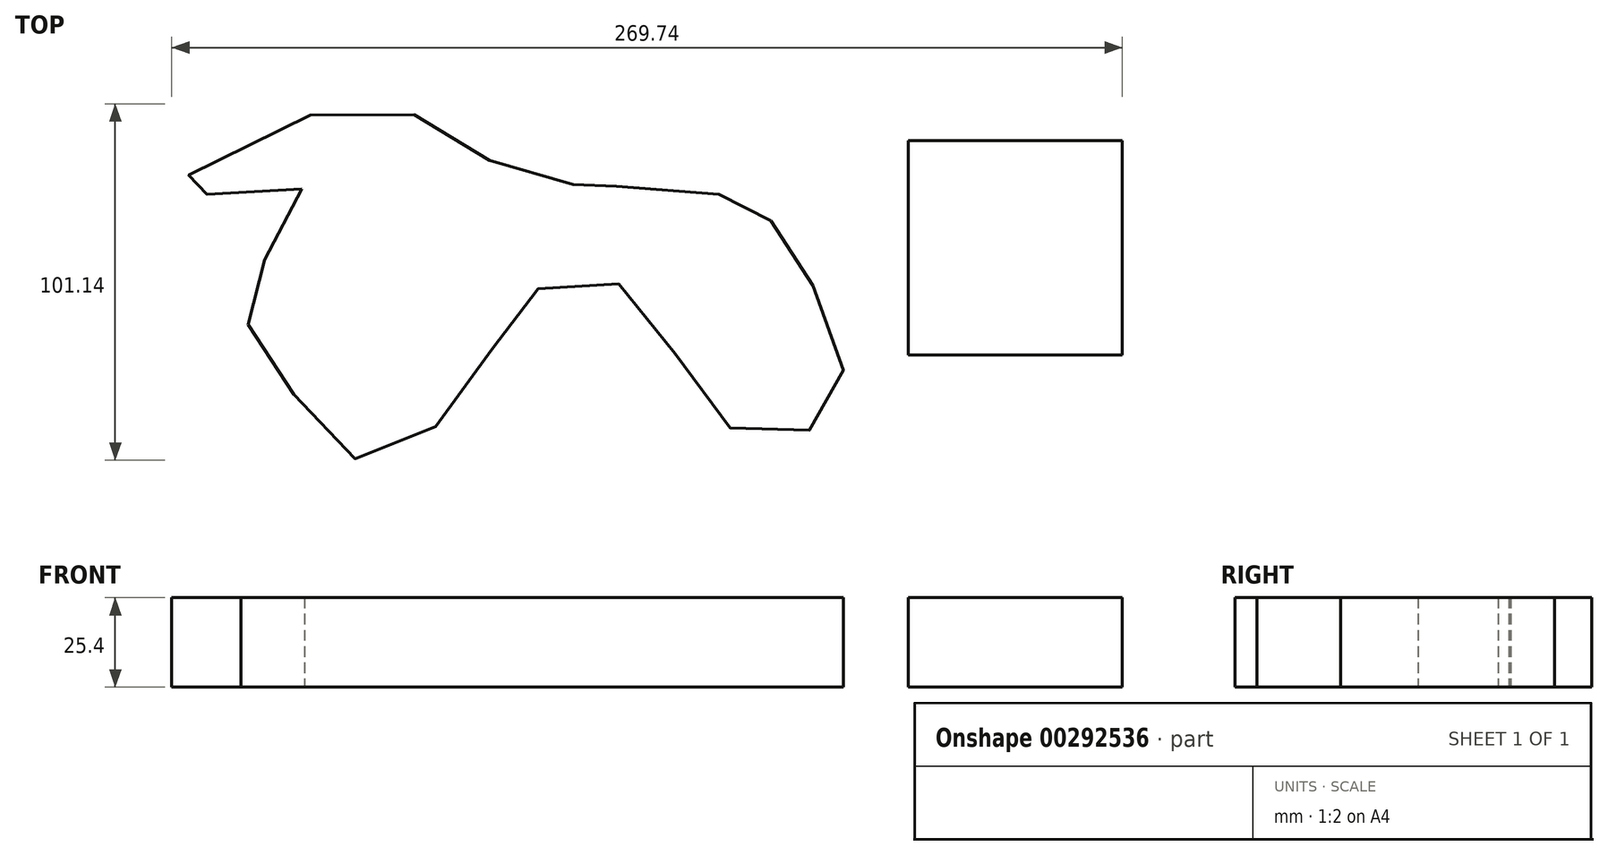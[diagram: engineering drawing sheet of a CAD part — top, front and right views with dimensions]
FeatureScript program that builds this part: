
annotation { "Feature Type Name" : "Feature", "Feature Type Description" : "" }
export const myFeature = defineFeature(function(context is Context, id is Id, definition is map)
    precondition{}
    {
        {
            var Q0;
            Q0=qCreatedBy(makeId("Top.planeOp"),FACE);
            var sketch = newSketch(context, id + "F0", { "sketchPlane" : qUnion([Q0])});
            skFitSpline(sketch, "E0", {"points": [v(-111.7, 29.63) * mm, v(-128.24, 0) * mm, v(-121.72, -15.73) * mm, v(-97, -46.84) * mm, v(-64.12, -26.88) * mm, v(-46.78, 0) * mm, v(-17.3, 0) * mm, v(6.07, -35.6) * mm, v(34.65, -37.44) * mm, v(40.7, -13.66) * mm, v(22.68, 18.4) * mm, v(14.71, 26.35) * mm, v(-26.73, 30.42) * mm, v(-31.6, 30.5) * mm, v(-62.5, 39.7) * mm, v(-97.04, 53.54) * mm, v(-148.3, 27.8) * mm, v(-111.7, 29.63) * mm]});
            skSolve(sketch);
        }
        {
            var Q0;
            Q0=makeQuery(id+"F0.imprint","IMPRINT",FACE,{"disambiguationData":[TD([[makeQuery(id+"F0.imprint","IMPRINT",EDGE,{"derivedFrom":sQuery(id+"F0.wireOp",EDGE,"E0")}),1.0]])]});
            extrude(context, id + "F1", {"entities" : qUnion([Q0]), "depth" : 25.4 * mm});
        }
        {
            var Q0;
            Q0=qCreatedBy(makeId("Top.planeOp"),FACE);
            var sketch = newSketch(context, id + "F2", { "sketchPlane" : qUnion([Q0])});
            skLineSegment(sketch, "E1.bottom", {"start": v(121.1, -17.45) * mm, "end": v(60.33, -17.45) * mm});
            skLineSegment(sketch, "E1.top", {"start": v(121.1, 43.31) * mm, "end": v(60.33, 43.31) * mm});
            skLineSegment(sketch, "E1.left", {"start": v(121.1, -17.45) * mm, "end": v(121.1, 43.31) * mm});
            skLineSegment(sketch, "E1.right", {"start": v(60.33, -17.45) * mm, "end": v(60.33, 43.31) * mm});
            skSolve(sketch);
        }
        {
            var Q0;
            Q0=makeQuery(id+"F2.imprint","IMPRINT",FACE,{"disambiguationData":[TD([[makeQuery(id+"F2.imprint","IMPRINT",EDGE,{"derivedFrom":sQuery(id+"F2.wireOp",EDGE,"E1.bottom")}),-1.0]])]});
            extrude(context, id + "F3", {"entities" : qUnion([Q0]), "depth" : 25.4 * mm});
        }
    });
